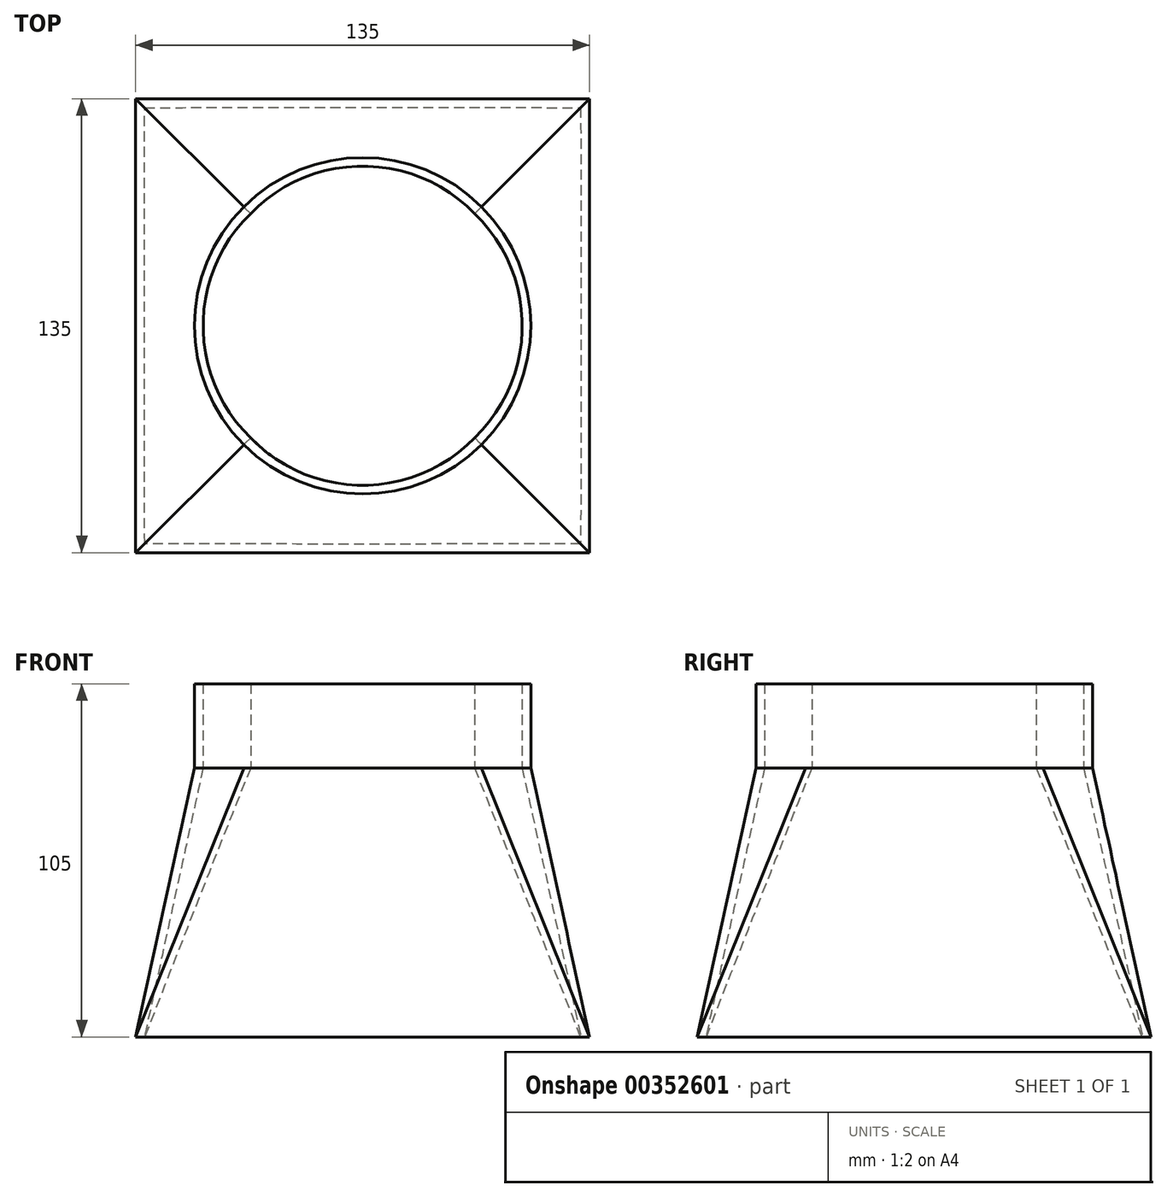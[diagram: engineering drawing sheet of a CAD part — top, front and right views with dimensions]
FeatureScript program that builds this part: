
annotation { "Feature Type Name" : "Feature", "Feature Type Description" : "" }
export const myFeature = defineFeature(function(context is Context, id is Id, definition is map)
    precondition{}
    {
        {
            var Q0;
            Q0=qCreatedBy(makeId("Top.planeOp"),FACE);
            var sketch = newSketch(context, id + "F0", { "sketchPlane" : qUnion([Q0])});
            skLineSegment(sketch, "E0.bottom", {"start": v(-67.5, -67.5) * mm, "end": v(67.5, -67.5) * mm});
            skLineSegment(sketch, "E0.top", {"start": v(-67.5, 67.5) * mm, "end": v(67.5, 67.5) * mm});
            skLineSegment(sketch, "E0.left", {"start": v(-67.5, -67.5) * mm, "end": v(-67.5, 67.5) * mm});
            skLineSegment(sketch, "E0.right", {"start": v(67.5, -67.5) * mm, "end": v(67.5, 67.5) * mm});
            skPoint(sketch, "E0.middle", {"position": v(0, 0) * mm});
            skLineSegment(sketch, "E1", {"start": v(0, 74.24) * mm, "end": v(0, -76.82) * mm, "construction": true});
            skSolve(sketch);
        }
        {
            var Q0;
            Q0=qCreatedBy(makeId("Top.planeOp"),FACE);
            cPlane(context, id + "F1", {"entities" : qUnion([Q0]), "cplaneType" : CPlaneType.OFFSET, "offset" : 80 * mm, "width" : 150 * mm, "height" : 150 * mm});
        }
        {
            var Q0;
            Q0=qCreatedBy(id+"F1.planeOp",FACE);
            var sketch = newSketch(context, id + "F2", { "sketchPlane" : qUnion([Q0])});
            skCircle(sketch, "E2", {"center": v(0, 0) * mm, "radius": 50 * mm});
            skSolve(sketch);
        }
        {
            var Q0;
            Q0=makeQuery(id+"F2.imprint","IMPRINT",FACE,{"disambiguationData":[TD([[makeQuery(id+"F2.imprint","IMPRINT",EDGE,{"derivedFrom":sQuery(id+"F2.wireOp",EDGE,"E2")}),1.0]])]});
            var Q1;
            Q1=makeQuery(id+"F0.imprint","IMPRINT",FACE,{"disambiguationData":[TD([[makeQuery(id+"F0.imprint","IMPRINT",EDGE,{"derivedFrom":sQuery(id+"F0.wireOp",EDGE,"E0.bottom")}),1.0]])]});
            loft(context, id + "F3", {"sheetProfilesArray" : [{ "sheetProfileEntities" : qUnion([Q0]) }, { "sheetProfileEntities" : qUnion([Q1]) }]});
        }
        {
            var Q0;
            Q0=makeQuery(id+"F3.opLoft","CAP_FACE",FACE,{"disambiguationData":[OSD([makeQuery(id+"F2.imprint","IMPRINT",FACE,{"disambiguationData":[TD([[makeQuery(id+"F2.imprint","IMPRINT",EDGE,{"derivedFrom":sQuery(id+"F2.wireOp",EDGE,"E2")}),1.0]])]})])],"isStart":true});
            var Q1;
            Q1=makeQuery(id+"F3.opLoft","CAP_FACE",FACE,{"disambiguationData":[OSD([makeQuery(id+"F0.imprint","IMPRINT",FACE,{"disambiguationData":[TD([[makeQuery(id+"F0.imprint","IMPRINT",EDGE,{"derivedFrom":sQuery(id+"F0.wireOp",EDGE,"E0.bottom")}),1.0]])]})])],"isStart":true});
            shell(context, id + "F4", {"entities" : qUnion([Q0, Q1]), "thickness" : 2.5 * mm});
        }
        {
            var Q0;
            Q0=makeQuery(id+"F3.opLoft","CAP_FACE",FACE,{"disambiguationData":[OSD([makeQuery(id+"F2.imprint","IMPRINT",FACE,{"disambiguationData":[TD([[makeQuery(id+"F2.imprint","IMPRINT",EDGE,{"derivedFrom":sQuery(id+"F2.wireOp",EDGE,"E2")}),1.0]])]})])],"isStart":true});
            extrude(context, id + "F5", {"entities" : qUnion([Q0]), "operationType" : NewBodyOperationType.ADD, "depth" : 25 * mm});
        }
    });
